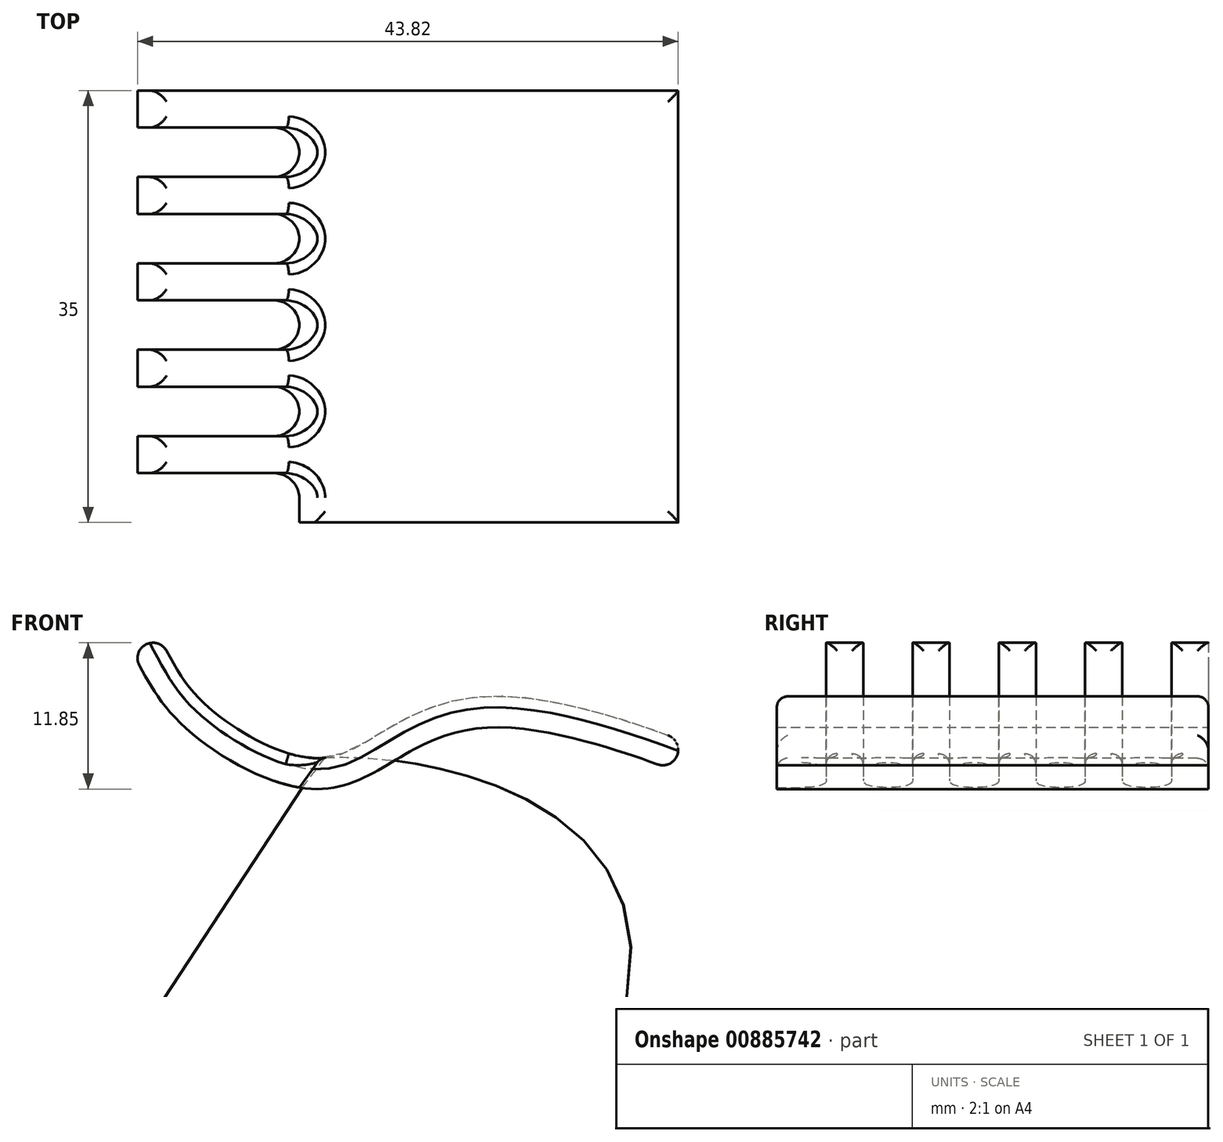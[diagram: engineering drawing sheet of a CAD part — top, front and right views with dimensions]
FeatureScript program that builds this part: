
annotation { "Feature Type Name" : "Feature", "Feature Type Description" : "" }
export const myFeature = defineFeature(function(context is Context, id is Id, definition is map)
    precondition{}
    {
        {
            var Q0;
            Q0=qCreatedBy(makeId("Front.planeOp"),FACE);
            var sketch = newSketch(context, id + "F0", { "sketchPlane" : qUnion([Q0])});
            skPoint(sketch, "E0.middle", {"position": v(0, 0) * mm});
            skFitSpline(sketch, "E1", {"points": [v(-21, 7.5) * mm, v(-17.3, 2.5) * mm, v(-6.5, -2.5) * mm, v(1.26, 0.72) * mm, v(8, 2.5) * mm, v(16.51, 0.99) * mm, v(21, -0.5) * mm], "startDerivative": vector(17.88, -32.54) * mm, "endDerivative": vector(30.73, -11.02) * mm});
            skFitSpline(sketch, "E2.0", {"points": [v(-18.8, 8.7) * mm, v(-18.62, 8.37) * mm, v(-18.27, 7.72) * mm, v(-17.72, 6.81) * mm, v(-17.12, 5.95) * mm, v(-16.39, 5.08) * mm, v(-15.46, 4.17) * mm, v(-14.27, 3.2) * mm, v(-12.88, 2.25) * mm, v(-11.37, 1.4) * mm, v(-9.83, 0.7) * mm, v(-8.6, 0.3) * mm, v(-7.68, 0.1) * mm, v(-7.15, 0.02) * mm, v(-6.76, 0) * mm, v(-6.48, 0) * mm, v(-6.22, 0.01) * mm, v(-5.69, 0.06) * mm, v(-4.9, 0.25) * mm, v(-3.79, 0.7) * mm, v(-2.61, 1.33) * mm, v(-1.57, 1.96) * mm, v(-0.7, 2.49) * mm, v(0, 2.88) * mm, v(0.71, 3.26) * mm, v(1.67, 3.71) * mm, v(2.91, 4.2) * mm, v(4.46, 4.64) * mm, v(6.08, 4.92) * mm, v(7.48, 5.01) * mm, v(8.63, 5) * mm, v(9.78, 4.93) * mm, v(11.22, 4.76) * mm, v(12.92, 4.46) * mm, v(14.56, 4.1) * mm, v(16.1, 3.7) * mm, v(17.5, 3.31) * mm, v(18.73, 2.93) * mm, v(20.22, 2.44) * mm, v(21.2, 2.08) * mm, v(21.84, 1.85) * mm]});
            skArc(sketch, "E3", {"start": v(-18.8, 8.7) * mm, "mid": v(-20.5, 9.2) * mm, "end": v(-21, 7.5) * mm});
            skArc(sketch, "E4", {"start": v(21, -0.5) * mm, "mid": v(22.6, 0.25) * mm, "end": v(21.84, 1.85) * mm});
            skArc(sketch, "E5", {"start": v(21, -0.5) * mm, "mid": v(11.4, 4.42) * mm, "end": v(1.26, 0.72) * mm});
            skArc(sketch, "E6.0", {"start": v(23.01, 1.15) * mm, "mid": v(11.56, 7.01) * mm, "end": v(-0.53, 2.6) * mm});
            skSolve(sketch);
        }
        {
            var Q0;
            Q0 = qSketchRegion(id + "F0", true);
            extrude(context, id + "F1", {"entities" : qUnion([Q0]), "endBound" : BoundingType.SYMMETRIC, "depth" : 35 * mm, "offsetDistance" : 25 * mm});
        }
        {
            var Q0;
            Q0=qCreatedBy(makeId("Front.planeOp"),FACE);
            var sketch = newSketch(context, id + "F2", { "sketchPlane" : qUnion([Q0])});
            skLineSegment(sketch, "E7", {"start": v(-10.54, -2.75) * mm, "end": v(-21.32, -2.75) * mm});
            skLineSegment(sketch, "E8", {"start": v(-21.32, 5) * mm, "end": v(-21.32, -2.75) * mm});
            skLineSegment(sketch, "E9", {"start": v(-10.54, -2.75) * mm, "end": v(-21.32, 5) * mm});
            skSolve(sketch);
        }
        {
            var Q0;
            Q0 = qSketchRegion(id + "F2", true);
            extrude(context, id + "F3", {"entities" : qUnion([Q0]), "operationType" : NewBodyOperationType.ADD, "endBound" : BoundingType.SYMMETRIC, "depth" : 50 * mm, "offsetDistance" : 25 * mm});
        }
        {
            var Q0;
            Q0=makeQuery(id+"F3.opExtrude","SWEPT_FACE",FACE,{"disambiguationData":[OSD([sQuery(id+"F2.wireOp",EDGE,"E9")])]});
            var sketch = newSketch(context, id + "F4", { "sketchPlane" : qUnion([Q0])});
            skPoint(sketch, "E10.endSnap0", {"position": v(-6.95, 0) * mm});
            skLineSegment(sketch, "E11.0", {"start": v(-7.14, -17.5) * mm, "end": v(-60.41, -17.5) * mm});
            skLineSegment(sketch, "E12.0", {"start": v(-7.14, 14.5) * mm, "end": v(-60.41, 14.5) * mm});
            skLineSegment(sketch, "E13.0", {"start": v(-7.14, 10.5) * mm, "end": v(-60.41, 10.5) * mm});
            skLineSegment(sketch, "E14.0", {"start": v(-7.14, 7.5) * mm, "end": v(-60.41, 7.5) * mm});
            skLineSegment(sketch, "E15.0", {"start": v(-7.14, 3.5) * mm, "end": v(-60.41, 3.5) * mm});
            skLineSegment(sketch, "E16.0", {"start": v(-7.14, 0.5) * mm, "end": v(-60.41, 0.5) * mm});
            skLineSegment(sketch, "E17.0", {"start": v(-7.14, -3.5) * mm, "end": v(-60.41, -3.5) * mm});
            skLineSegment(sketch, "E18.0", {"start": v(-7.14, -6.5) * mm, "end": v(-60.41, -6.5) * mm});
            skLineSegment(sketch, "E19.0", {"start": v(-7.14, -10.5) * mm, "end": v(-60.41, -10.5) * mm});
            skLineSegment(sketch, "E20.0", {"start": v(-7.14, -13.5) * mm, "end": v(-60.41, -13.5) * mm});
            skLineSegment(sketch, "E21", {"start": v(-60.41, -17.5) * mm, "end": v(-60.41, -13.5) * mm});
            skLineSegment(sketch, "E22", {"start": v(-60.41, -10.5) * mm, "end": v(-60.41, -6.5) * mm});
            skLineSegment(sketch, "E23", {"start": v(-60.41, -3.5) * mm, "end": v(-60.41, 0.5) * mm});
            skLineSegment(sketch, "E24", {"start": v(-60.41, 3.5) * mm, "end": v(-60.41, 7.5) * mm});
            skLineSegment(sketch, "E25", {"start": v(-60.41, 10.5) * mm, "end": v(-60.41, 14.5) * mm});
            skArc(sketch, "E26", {"start": v(-5.14, -15.5) * mm, "mid": v(-5.72, -14.09) * mm, "end": v(-7.14, -13.5) * mm});
            skArc(sketch, "E27", {"start": v(-7.14, -10.5) * mm, "mid": v(-5.14, -8.5) * mm, "end": v(-7.14, -6.5) * mm});
            skArc(sketch, "E28", {"start": v(-7.14, -3.5) * mm, "mid": v(-5.14, -1.5) * mm, "end": v(-7.14, 0.5) * mm});
            skArc(sketch, "E29", {"start": v(-7.14, 3.5) * mm, "mid": v(-5.14, 5.5) * mm, "end": v(-7.14, 7.5) * mm});
            skArc(sketch, "E30", {"start": v(-7.14, 10.5) * mm, "mid": v(-5.14, 12.5) * mm, "end": v(-7.14, 14.5) * mm});
            skLineSegment(sketch, "E31", {"start": v(-5.14, -15.5) * mm, "end": v(-5.14, -17.5) * mm});
            skLineSegment(sketch, "E32", {"start": v(-7.14, -17.5) * mm, "end": v(-5.14, -17.5) * mm});
            skSolve(sketch);
        }
        {
            var Q0;
            Q0 = qSketchRegion(id + "F4", true);
            extrude(context, id + "F5", {"entities" : qUnion([Q0]), "operationType" : NewBodyOperationType.REMOVE, "depth" : 25 * mm, "offsetDistance" : 25 * mm});
        }
        {
            var Q0;
            Q0=makeQuery(id+"F1.opExtrude","SWEPT_FACE",FACE,{"disambiguationData":[OSD([sQuery(id+"F0.wireOp",EDGE,"E2.0")])]});
            fillet(context, id + "F6", {"entities" : qUnion([Q0]), "radius" : .9 * mm, "tangentPropagation" : true, "allowEdgeOverflow" : false});
        }
        {
            var Q0;
            Q0=makeQuery(id+"F3.opExtrude","SWEPT_BODY",BODY,{"disambiguationData":[OSD([sQuery(id+"F2.wireOp",EDGE,"E7"),sQuery(id+"F2.wireOp",EDGE,"E8"),sQuery(id+"F2.wireOp",EDGE,"E9")])]});
            deleteBodies(context, id + "F7", {"entities" : qUnion([Q0])});
        }
    });
